# Revit family: Шлагбаум PERCo-GS04-1
name_source: partatom
category: Электрические приборы
units: mm (PartAtom-declared; Revit-internal decimal feet)

## family parameters
Всегда вертикально = Да
На основе рабочей плоскости = Нет
Общий = Нет
При загрузке вырезать с полостями = Нет
Размер круглого соединителя = Использовать диаметр
Сохранять ориентацию аннотаций = Нет
Тип детали = Нормальный
Точка расчета площади = Нет

## types (6) — shared parameters
A = 330 мм
ADSK_URL страницы изделия = https://www.perco.ru
ADSK_Единица измерения = шт.
ADSK_Завод-изготовитель = ООО «ПЭРКо»
ADSK_Количество = 1
ADSK_Количество фаз = 1
ADSK_Масса_Текст = 54 кг
ADSK_Материал наименование = Сталь, алюминий
ADSK_Наименование = Шлагбаум PERCo-GS04
ADSK_Наименование краткое = PERCo-GS04
ADSK_Напряжение = 24 В
ADSK_Номинальная мощность = 175 Вт
ADSK_Ток = 7 А
B = 287 мм
H = 1070 мм
H1 = 880 мм
PERCo_Пропускная способность = 7000 ТС/сутки
PERCo_Степень защиты от внешней среды = IP 54
PERCo_Температура использования = От -40⁰С до +55⁰С
h1 = 970 мм
h2 = 70 мм
h3 = 30 мм
h4 = 520 мм
Материал = Алюминий 5052
Материал двери = Сталь, окрашенная, темно-серая, матовая
Материал_индикатор = Пластмасса, прозрачная(1)
zero-valued in all types: ADSK_Количество фаз числовое, ADSK_Коэффициент мощности

## per-type parameters (varying)
| type | PERCo_Габариты | q | Типа стрелы |
| Прямоугольно-овальная стрела 4,3 м | 370×4400×1070 мм | 27 мм | Стрела прямоугольно-овальная : Тип 1 |
| Прямоугольно-овальная стрела 3 м | 370×3100×1070 | 27 мм | Стрела прямоугольно-овальная : Тип 2 |
| Круглая стрела 4,3 м | 405×4400×1070 мм | 43 мм | Стрела  круглая : Тип 1 |
| Круглая стрела 3 м | 405×3100×1070 | 43 мм | Стрела  круглая : Тип 2 |
| Прямоугольно-овальная стрела складная 3 м | 390×3100×1070 | 27 мм | Стрела прямоугольно-овальная складная : Тип 2 |
| Прямоугольно-овальная стрела складная 4,3 м | 390×4400×1070 | 27 мм | Стрела прямоугольно-овальная складная : Тип 1 |
